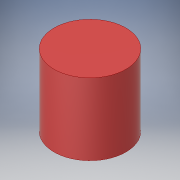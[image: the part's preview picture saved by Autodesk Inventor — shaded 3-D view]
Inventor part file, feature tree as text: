
AUTODESK INVENTOR PART (.ipt)
format: ipt  version: 2019.3 (Build 233278000, 278)  size: 205,312 bytes
history: native  units: mm
features: extrude x1, sketch x1
ambient origin geometry x8: Origin, YZ Plane, XZ Plane, XY Plane, X Axis, Y Axis, Z Axis, Center Point
bodies: Solide1 (feature_tree)
feature tree (2):
  extrude  "Cylindre1"  Depth=40.0mm
  sketch  "Esquisse1"
